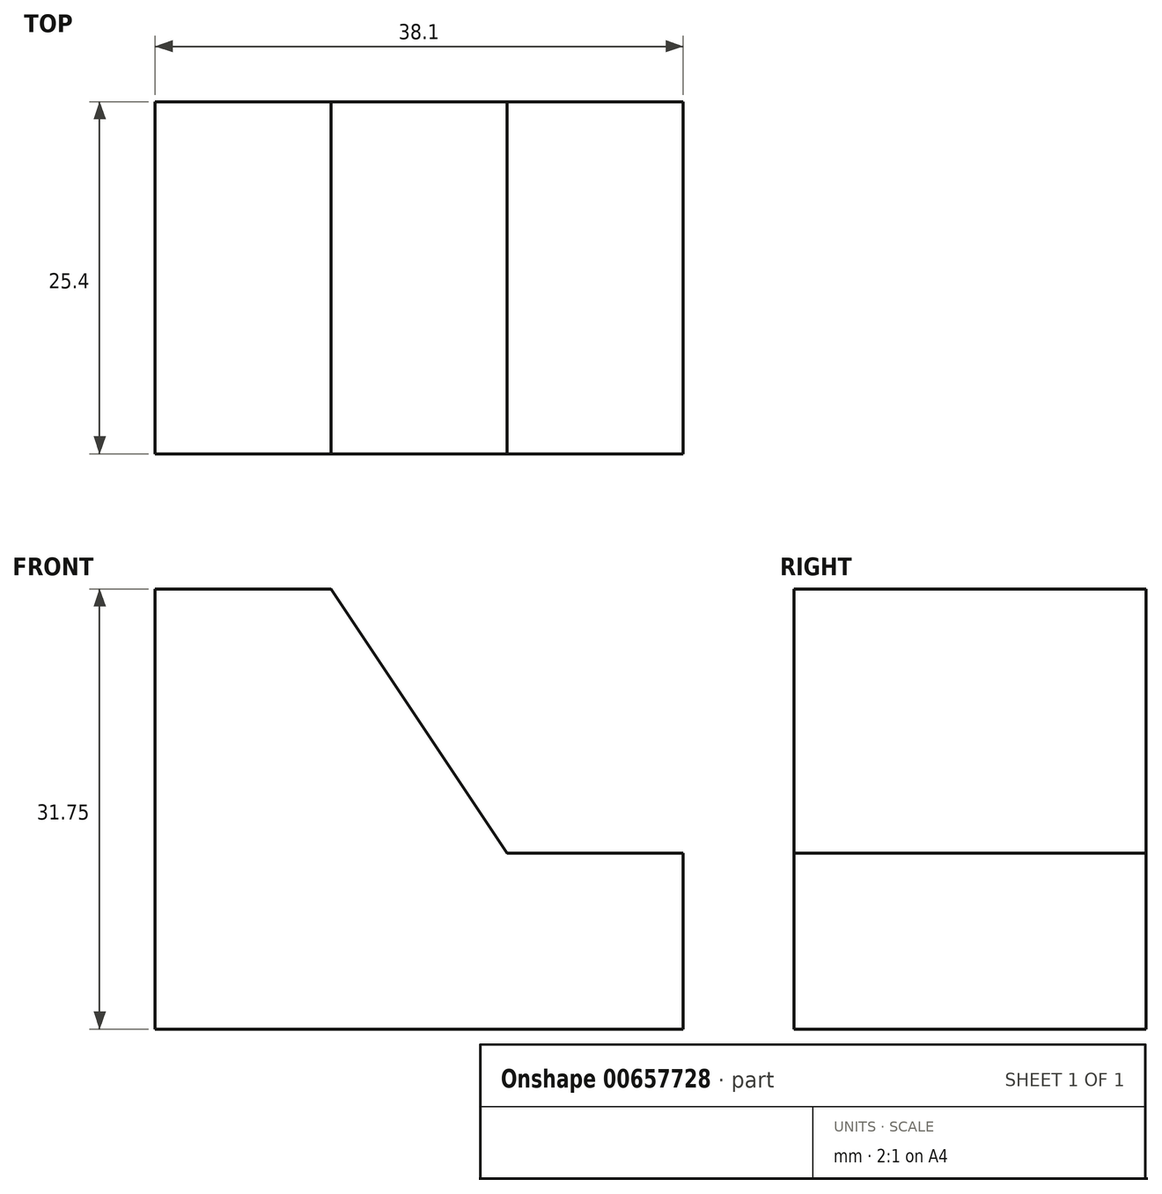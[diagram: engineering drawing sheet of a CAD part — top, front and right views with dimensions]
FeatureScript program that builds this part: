
annotation { "Feature Type Name" : "Feature", "Feature Type Description" : "" }
export const myFeature = defineFeature(function(context is Context, id is Id, definition is map)
    precondition{}
    {
        {
            var Q0;
            Q0=qCreatedBy(makeId("Front.planeOp"),FACE);
            var sketch = newSketch(context, id + "F0", { "sketchPlane" : qUnion([Q0])});
            skLineSegment(sketch, "E0", {"start": v(0, 0) * mm, "end": v(-38.1, 0) * mm});
            skLineSegment(sketch, "E1", {"start": v(-38.1, 0) * mm, "end": v(-38.1, 31.75) * mm});
            skLineSegment(sketch, "E2", {"start": v(-38.1, 31.75) * mm, "end": v(-25.4, 31.75) * mm});
            skLineSegment(sketch, "E3", {"start": v(0, 0) * mm, "end": v(0, 12.7) * mm});
            skLineSegment(sketch, "E4", {"start": v(0, 12.7) * mm, "end": v(-12.7, 12.7) * mm});
            skLineSegment(sketch, "E5", {"start": v(-12.7, 12.7) * mm, "end": v(-25.4, 31.75) * mm});
            skSolve(sketch);
        }
        {
            var Q0;
            Q0=makeQuery(id+"F0.imprint","IMPRINT",FACE,{"disambiguationData":[TD([[makeQuery(id+"F0.imprint","IMPRINT",EDGE,{"derivedFrom":sQuery(id+"F0.wireOp",EDGE,"E0")}),-1.0]])]});
            extrude(context, id + "F1", {"entities" : qUnion([Q0]), "depth" : 25.4 * mm, "offsetDistance" : 25.4 * mm});
        }
    });
